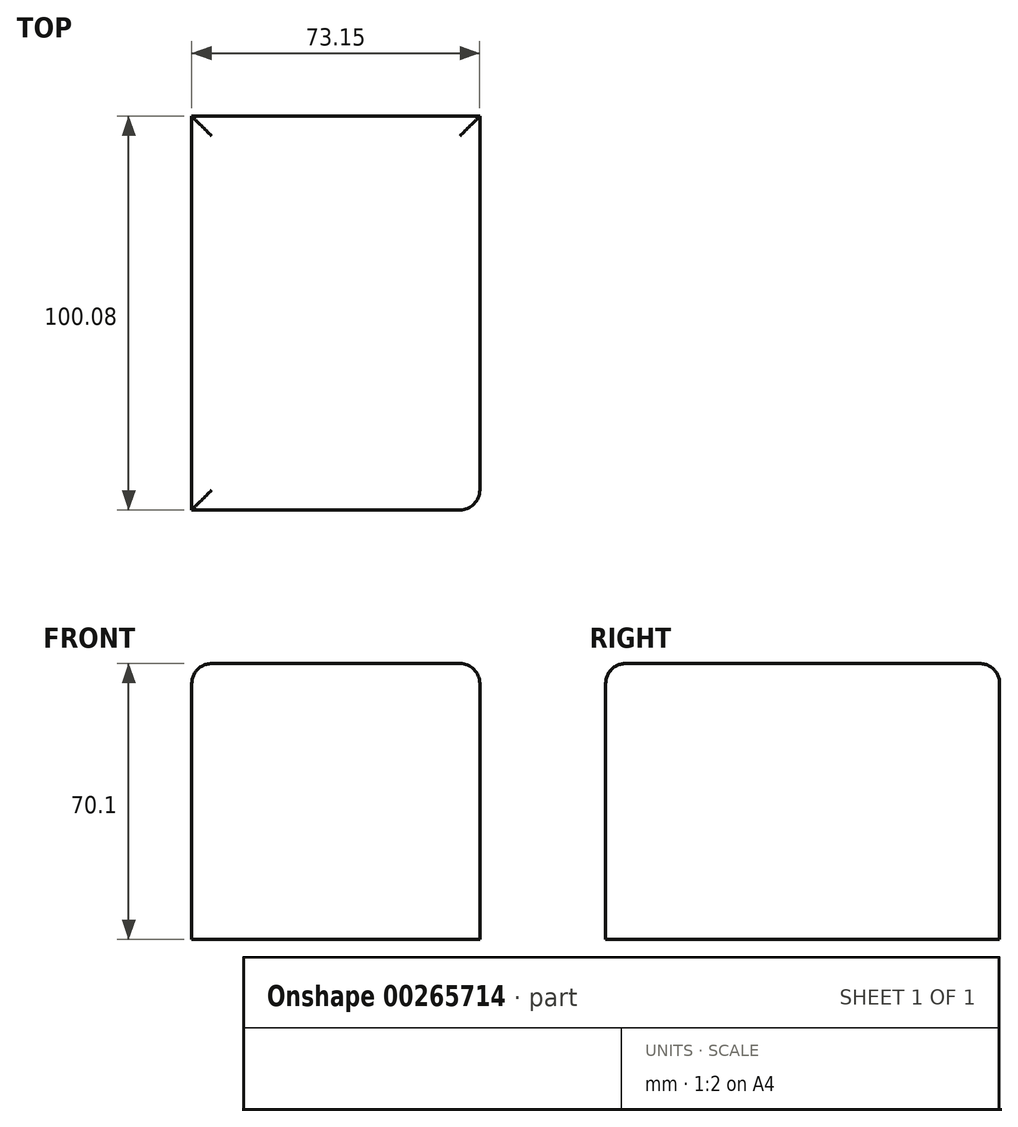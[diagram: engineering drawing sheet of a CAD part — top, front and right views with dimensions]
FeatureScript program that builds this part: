
annotation { "Feature Type Name" : "Feature", "Feature Type Description" : "" }
export const myFeature = defineFeature(function(context is Context, id is Id, definition is map)
    precondition{}
    {
        {
            var Q0;
            Q0=qCreatedBy(makeId("Front.planeOp"),FACE);
            var sketch = newSketch(context, id + "F0", { "sketchPlane" : qUnion([Q0])});
            skLineSegment(sketch, "E0.bottom", {"start": v(-37.34, 34.3) * mm, "end": v(35.81, 34.3) * mm});
            skLineSegment(sketch, "E0.top", {"start": v(-37.34, -35.81) * mm, "end": v(35.81, -35.81) * mm});
            skLineSegment(sketch, "E0.left", {"start": v(-37.34, 34.3) * mm, "end": v(-37.34, -35.81) * mm});
            skLineSegment(sketch, "E0.right", {"start": v(35.81, 34.3) * mm, "end": v(35.81, -35.81) * mm});
            skSolve(sketch);
        }
        {
            var Q0;
            Q0=makeQuery(id+"F0.imprint","IMPRINT",FACE,{"disambiguationData":[TD([[makeQuery(id+"F0.imprint","IMPRINT",EDGE,{"derivedFrom":sQuery(id+"F0.wireOp",EDGE,"E0.bottom")}),-1.0]])]});
            extrude(context, id + "F1", {"entities" : qUnion([Q0]), "depth" : 100.08 * mm});
        }
        {
            var Q0;
            Q0=makeQuery(id+"F1.opExtrude","SWEPT_EDGE",EDGE,{"disambiguationData":[OSD([sQuery(id+"F0.wireOp",EDGE,"E0.bottom"),sQuery(id+"F0.wireOp",EDGE,"E0.left")])]});
            var Q1;
            Q1=makeQuery(id+"F1.opExtrude","CAP_EDGE",EDGE,{"disambiguationData":[OSD([sQuery(id+"F0.wireOp",EDGE,"E0.bottom")])],"isStart":false});
            var Q2;
            Q2=makeQuery(id+"F1.opExtrude","SWEPT_EDGE",EDGE,{"disambiguationData":[OSD([sQuery(id+"F0.wireOp",EDGE,"E0.bottom"),sQuery(id+"F0.wireOp",EDGE,"E0.right")])]});
            var Q3;
            Q3=makeQuery(id+"F1.opExtrude","CAP_EDGE",EDGE,{"disambiguationData":[OSD([sQuery(id+"F0.wireOp",EDGE,"E0.bottom")])],"isStart":true});
            var Q4;
            Q4=makeQuery(id+"F1.opExtrude","CAP_EDGE",EDGE,{"disambiguationData":[OSD([sQuery(id+"F0.wireOp",EDGE,"E0.right")])],"isStart":false});
            fillet(context, id + "F2", {"entities" : qUnion([Q0, Q1, Q2, Q3, Q4]), "radius" : 5.08 * mm, "tangentPropagation" : true, "allowEdgeOverflow" : false});
        }
    });
